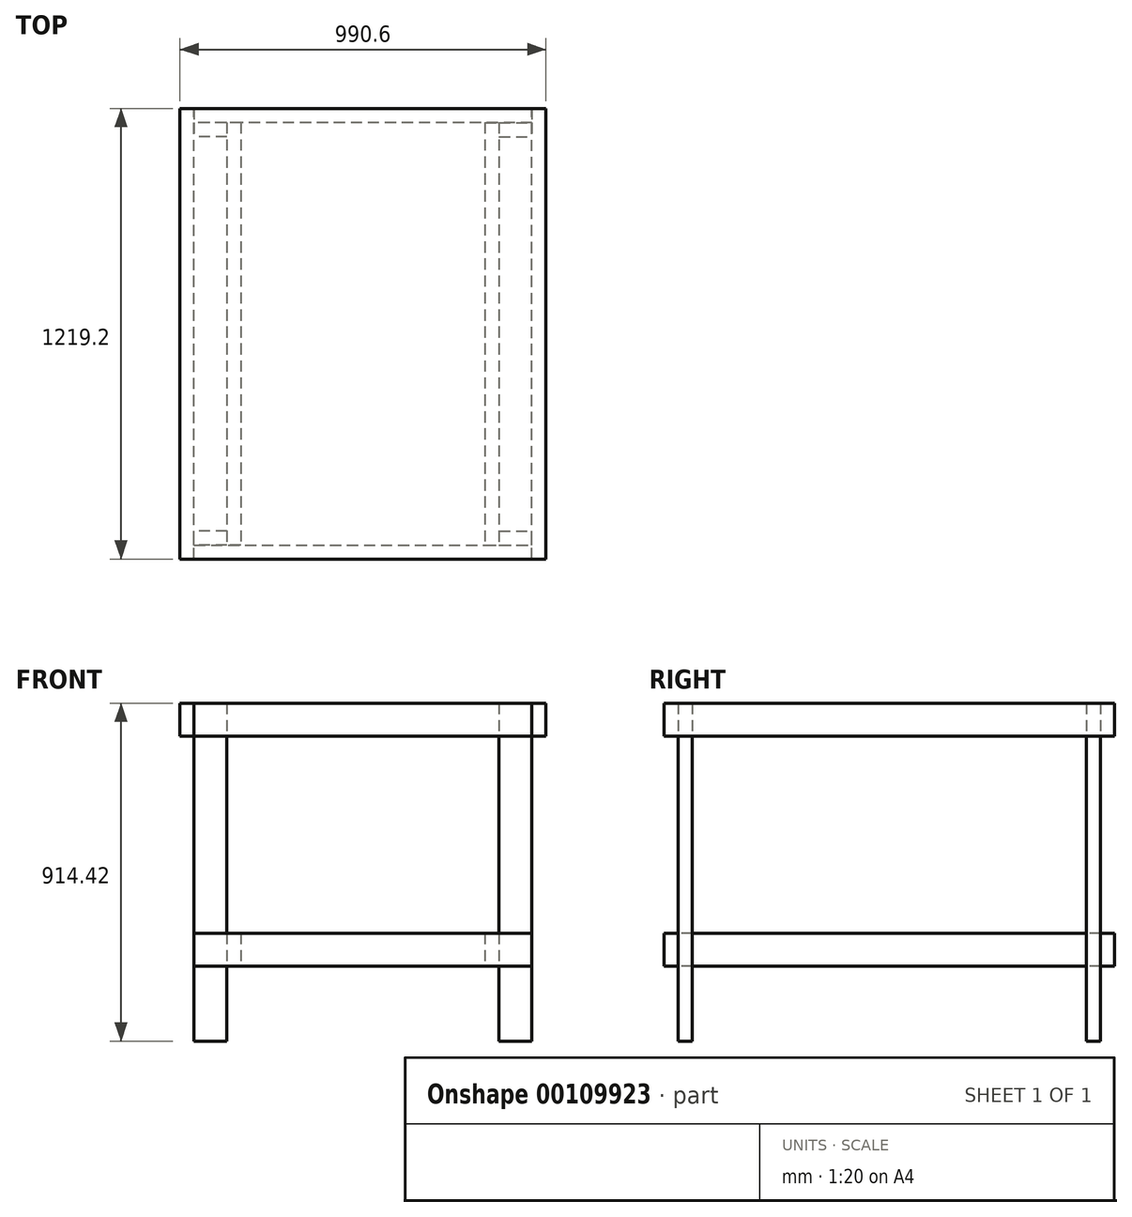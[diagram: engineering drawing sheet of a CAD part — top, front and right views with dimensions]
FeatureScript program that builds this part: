
annotation { "Feature Type Name" : "Feature", "Feature Type Description" : "" }
export const myFeature = defineFeature(function(context is Context, id is Id, definition is map)
    precondition{}
    {
        {
            assignVariable(context, id + "F0", {"name" : "l", "anyValue" : 914.4 * mm});
        }
        {
            assignVariable(context, id + "F1", {"name" : "h", "anyValue" : 914.4 * mm});
        }
        {
            assignVariable(context, id + "F2", {"name" : "bw", "anyValue" : 88.9 * mm});
        }
        {
            assignVariable(context, id + "F3", {"name" : "bh", "anyValue" : 38.1 * mm});
        }
        {
            assignVariable(context, id + "F4", {"name" : "toph", "anyValue" : 5 / 203.2 * mm});
        }
        {
            assignVariable(context, id + "F5", {"name" : "mm", "anyValue" : 203.2 * mm});
        }
        {
            var Q0;
            Q0=qCreatedBy(makeId("Top.planeOp"),FACE);
            var sketch = newSketch(context, id + "F6", { "sketchPlane" : qUnion([Q0])});
            skLineSegment(sketch, "E0.bottom", {"start": v(330.2, 571.5) * mm, "end": v(-330.2, 571.5) * mm});
            skLineSegment(sketch, "E0.top", {"start": v(330.2, -571.5) * mm, "end": v(-330.2, -571.5) * mm});
            skLineSegment(sketch, "E0.left", {"start": v(330.2, 571.5) * mm, "end": v(330.2, -571.5) * mm});
            skLineSegment(sketch, "E0.right", {"start": v(-330.2, 571.5) * mm, "end": v(-330.2, -571.5) * mm});
            skPoint(sketch, "E0.middle", {"position": v(0, 0) * mm});
            skLineSegment(sketch, "E1.bottom", {"start": v(330.2, 571.5) * mm, "end": v(368.3, 571.5) * mm});
            skLineSegment(sketch, "E1.top", {"start": v(330.2, -571.5) * mm, "end": v(368.3, -571.5) * mm});
            skLineSegment(sketch, "E1.right", {"start": v(368.3, 571.5) * mm, "end": v(368.3, -571.5) * mm});
            skLineSegment(sketch, "E2.bottom", {"start": v(-330.2, 571.5) * mm, "end": v(-368.3, 571.5) * mm});
            skLineSegment(sketch, "E2.top", {"start": v(-330.2, -571.5) * mm, "end": v(-368.3, -571.5) * mm});
            skLineSegment(sketch, "E2.right", {"start": v(-368.3, 571.5) * mm, "end": v(-368.3, -571.5) * mm});
            skLineSegment(sketch, "E3.bottom", {"start": v(368.3, -571.5) * mm, "end": v(457.2, -571.5) * mm});
            skLineSegment(sketch, "E3.top", {"start": v(368.3, -533.4) * mm, "end": v(457.2, -533.4) * mm});
            skLineSegment(sketch, "E3.left", {"start": v(368.3, -571.5) * mm, "end": v(368.3, -533.4) * mm});
            skLineSegment(sketch, "E3.right", {"start": v(457.2, -571.5) * mm, "end": v(457.2, -533.4) * mm});
            skLineSegment(sketch, "E4.bottom", {"start": v(368.3, 571.5) * mm, "end": v(457.2, 571.5) * mm});
            skLineSegment(sketch, "E4.top", {"start": v(368.3, 533.4) * mm, "end": v(457.2, 533.4) * mm});
            skLineSegment(sketch, "E4.left", {"start": v(368.3, 571.5) * mm, "end": v(368.3, 533.4) * mm});
            skLineSegment(sketch, "E4.right", {"start": v(457.2, 571.5) * mm, "end": v(457.2, 533.4) * mm});
            skLineSegment(sketch, "E5.bottom", {"start": v(-368.3, 571.5) * mm, "end": v(-457.2, 571.5) * mm});
            skLineSegment(sketch, "E5.top", {"start": v(-368.3, 533.4) * mm, "end": v(-457.2, 533.4) * mm});
            skLineSegment(sketch, "E5.left", {"start": v(-368.3, 571.5) * mm, "end": v(-368.3, 533.4) * mm});
            skLineSegment(sketch, "E5.right", {"start": v(-457.2, 571.5) * mm, "end": v(-457.2, 533.4) * mm});
            skLineSegment(sketch, "E6.bottom", {"start": v(-368.3, -571.5) * mm, "end": v(-457.2, -571.5) * mm});
            skLineSegment(sketch, "E6.top", {"start": v(-368.3, -533.4) * mm, "end": v(-457.2, -533.4) * mm});
            skLineSegment(sketch, "E6.left", {"start": v(-368.3, -571.5) * mm, "end": v(-368.3, -533.4) * mm});
            skLineSegment(sketch, "E6.right", {"start": v(-457.2, -571.5) * mm, "end": v(-457.2, -533.4) * mm});
            skLineSegment(sketch, "E7.bottom", {"start": v(-457.2, 609.6) * mm, "end": v(457.2, 609.6) * mm});
            skLineSegment(sketch, "E7.top", {"start": v(-457.2, 571.5) * mm, "end": v(457.2, 571.5) * mm});
            skLineSegment(sketch, "E7.left", {"start": v(-457.2, 609.6) * mm, "end": v(-457.2, 571.5) * mm});
            skLineSegment(sketch, "E7.right", {"start": v(457.2, 609.6) * mm, "end": v(457.2, 571.5) * mm});
            skLineSegment(sketch, "E8.bottom", {"start": v(-457.2, -609.6) * mm, "end": v(457.2, -609.6) * mm});
            skLineSegment(sketch, "E8.top", {"start": v(-457.2, -571.5) * mm, "end": v(457.2, -571.5) * mm});
            skLineSegment(sketch, "E8.left", {"start": v(-457.2, -609.6) * mm, "end": v(-457.2, -571.5) * mm});
            skLineSegment(sketch, "E8.right", {"start": v(457.2, -609.6) * mm, "end": v(457.2, -571.5) * mm});
            skSolve(sketch);
        }
        {
            var Q0;
            Q0=makeQuery(id+"F6.imprint","IMPRINT",FACE,{"disambiguationData":[TD([[makeQuery(id+"F6.imprint","IMPRINT",EDGE,{"derivedFrom":sQuery(id+"F6.wireOp",EDGE,"E3.top")}),-1.0]])]});
            var Q1;
            Q1=makeQuery(id+"F6.imprint","IMPRINT",FACE,{"disambiguationData":[TD([[makeQuery(id+"F6.imprint","IMPRINT",EDGE,{"derivedFrom":sQuery(id+"F6.wireOp",EDGE,"E4.top")}),1.0]])]});
            var Q2;
            Q2=makeQuery(id+"F6.imprint","IMPRINT",FACE,{"disambiguationData":[TD([[makeQuery(id+"F6.imprint","IMPRINT",EDGE,{"derivedFrom":sQuery(id+"F6.wireOp",EDGE,"E5.top")}),-1.0]])]});
            var Q3;
            Q3=makeQuery(id+"F6.imprint","IMPRINT",FACE,{"disambiguationData":[TD([[makeQuery(id+"F6.imprint","IMPRINT",EDGE,{"derivedFrom":sQuery(id+"F6.wireOp",EDGE,"E6.top")}),1.0]])]});
            extrude(context, id + "F7", {"entities" : qUnion([Q0, Q1, Q2, Q3]), "depth" : getVariable(context, 'h') - getVariable(context, 'mm'), "hasSecondDirection" : true, "secondDirectionOppositeDirection" : true, "secondDirectionDepth" : getVariable(context, 'mm')});
        }
        {
            var Q0;
            Q0=makeQuery(id+"F6.imprint","IMPRINT",FACE,{"disambiguationData":[TD([[makeQuery(id+"F6.imprint","IMPRINT",EDGE,{"derivedFrom":sQuery(id+"F6.wireOp",EDGE,"E7.bottom")}),-1.0]])]});
            var Q1;
            Q1=makeQuery(id+"F6.imprint","IMPRINT",FACE,{"disambiguationData":[TD([[makeQuery(id+"F6.imprint","IMPRINT",EDGE,{"derivedFrom":sQuery(id+"F6.wireOp",EDGE,"E8.bottom")}),1.0]])]});
            extrude(context, id + "F8", {"entities" : qUnion([Q0, Q1]), "depth" : getVariable(context, 'bw')});
        }
        {
            var Q0;
            {var subQ2=sQuery(id+"F6.wireOp",EDGE,"E0.right");Q0=makeQuery(id+"F6.imprint","IMPRINT",FACE,{"disambiguationData":[TD([[makeQuery(id+"F6.imprint","IMPRINT",EDGE,{"derivedFrom":subQ2}),-1.0]])]});}
            var Q1;
            {var subQ2=sQuery(id+"F6.wireOp",EDGE,"E0.left");Q1=makeQuery(id+"F6.imprint","IMPRINT",FACE,{"disambiguationData":[TD([[makeQuery(id+"F6.imprint","IMPRINT",EDGE,{"derivedFrom":subQ2}),1.0]])]});}
            extrude(context, id + "F9", {"entities" : qUnion([Q0, Q1]), "depth" : getVariable(context, 'bw')});
        }
        {
            var Q0;
            Q0=makeQuery(id+"F8.opExtrude","SWEPT_BODY",BODY,{"disambiguationData":[OSD([sQuery(id+"F6.wireOp",EDGE,"E7.bottom"),sQuery(id+"F6.wireOp",EDGE,"E7.top"),sQuery(id+"F6.wireOp",EDGE,"E7.left"),sQuery(id+"F6.wireOp",EDGE,"E7.right")])]});
            var Q1;
            Q1=makeQuery(id+"F8.opExtrude","SWEPT_BODY",BODY,{"disambiguationData":[OSD([sQuery(id+"F6.wireOp",EDGE,"E8.bottom"),sQuery(id+"F6.wireOp",EDGE,"E8.top"),sQuery(id+"F6.wireOp",EDGE,"E8.left"),sQuery(id+"F6.wireOp",EDGE,"E8.right")])]});
            var Q2;
            Q2=makeQuery(id+"F8.opExtrude","SWEPT_EDGE",EDGE,{"disambiguationData":[OSD([sQuery(id+"F6.wireOp",EDGE,"E8.bottom"),sQuery(id+"F6.wireOp",EDGE,"E8.left")])]});
            transform(context, id + "F10", {"entities" : qUnion([Q0, Q1]), "transformType" : TransformType.TRANSLATION_DISTANCE, "transformDirection" : qUnion([Q2]), "distance" : getVariable(context, 'h') - getVariable(context, 'mm') - getVariable(context, 'bw'), "oppositeDirection" : true, "makeCopy" : true});
        }
        {
            var Q0;
            Q0=makeQuery(id+"F10.opPattern","COPY",FACE,{"derivedFrom":makeQuery(id+"F8.opExtrude","SWEPT_FACE",FACE,{"disambiguationData":[OSD([sQuery(id+"F6.wireOp",EDGE,"E8.right")])]}),"instanceName":"1"});
            var sketch = newSketch(context, id + "F11", { "sketchPlane" : qUnion([Q0])});
            skLineSegment(sketch, "E9.bottom", {"start": v(-609.6, 711.2) * mm, "end": v(609.6, 711.2) * mm});
            skLineSegment(sketch, "E9.top", {"start": v(-609.6, 622.3) * mm, "end": v(609.6, 622.3) * mm});
            skLineSegment(sketch, "E9.left", {"start": v(-609.6, 711.2) * mm, "end": v(-609.6, 622.3) * mm});
            skLineSegment(sketch, "E9.right", {"start": v(609.6, 711.2) * mm, "end": v(609.6, 622.3) * mm});
            skSolve(sketch);
        }
        {
            var Q0;
            {var subQ2=sQuery(id+"F11.wireOp",EDGE,"E9.right");Q0=makeQuery(id+"F11.imprint","IMPRINT",FACE,{"disambiguationData":[TD([[makeQuery(id+"F11.imprint","IMPRINT",EDGE,{"derivedFrom":subQ2}),-1.0]])]});}
            var Q1;
            {var subQ2=sQuery(id+"F11.wireOp",EDGE,"E9.left");Q1=makeQuery(id+"F11.imprint","IMPRINT",FACE,{"disambiguationData":[TD([[makeQuery(id+"F11.imprint","IMPRINT",EDGE,{"derivedFrom":subQ2}),1.0]])]});}
            extrude(context, id + "F12", {"entities" : qUnion([Q0, Q1]), "depth" : getVariable(context, 'bh')});
        }
        {
            var Q0;
            Q0=makeQuery(id+"F12.opExtrude","SWEPT_BODY",BODY,{"disambiguationData":[OSD([sQuery(id+"F11.wireOp",EDGE,"E9.bottom"),sQuery(id+"F11.wireOp",EDGE,"E9.top"),sQuery(id+"F11.wireOp",EDGE,"E9.left"),sQuery(id+"F11.wireOp",EDGE,"E9.right")])]});
            var Q1;
            Q1=makeQuery(id+"F10.opPattern","COPY",EDGE,{"derivedFrom":makeQuery(id+"F8.opExtrude","CAP_EDGE",EDGE,{"disambiguationData":[OSD([sQuery(id+"F6.wireOp",EDGE,"E8.bottom")])],"isStart":false}),"instanceName":"1"});
            transform(context, id + "F13", {"entities" : qUnion([Q0]), "transformType" : TransformType.TRANSLATION_DISTANCE, "transformDirection" : qUnion([Q1]), "distance" : getVariable(context, 'l') + getVariable(context, 'bh'), "oppositeDirection" : true, "makeCopy" : true});
        }
        {
            var Q0;
            Q0=makeQuery(id+"F12.opExtrude","SWEPT_FACE",FACE,{"disambiguationData":[OSD([sQuery(id+"F11.wireOp",EDGE,"E9.bottom")])]});
            var sketch = newSketch(context, id + "F14", { "sketchPlane" : qUnion([Q0])});
            skLineSegment(sketch, "E10.0", {"start": v(-495.3, -609.6) * mm, "end": v(-495.3, 609.6) * mm});
            skLineSegment(sketch, "E11.bottom", {"start": v(-495.3, -609.6) * mm, "end": v(495.3, -609.6) * mm});
            skLineSegment(sketch, "E11.top", {"start": v(-495.3, 609.6) * mm, "end": v(495.3, 609.6) * mm});
            skLineSegment(sketch, "E11.right", {"start": v(495.3, -609.6) * mm, "end": v(495.3, 609.6) * mm});
            skSolve(sketch);
        }
        {
            var Q0;
            {var subQ2=sQuery(id+"F14.wireOp",EDGE,"E10.0");Q0=makeQuery(id+"F14.imprint","IMPRINT",FACE,{"disambiguationData":[TD([[makeQuery(id+"F14.imprint","IMPRINT",EDGE,{"derivedFrom":subQ2}),-1.0]])]});}
            var Q1;
            {var subQ2=sQuery(id+"F14.wireOp",EDGE,"E11.right");Q1=makeQuery(id+"F14.imprint","IMPRINT",FACE,{"disambiguationData":[TD([[makeQuery(id+"F14.imprint","IMPRINT",EDGE,{"derivedFrom":subQ2}),1.0]])]});}
            extrude(context, id + "F15", {"entities" : qUnion([Q0, Q1]), "depth" : getVariable(context, 'toph')});
        }
    });
